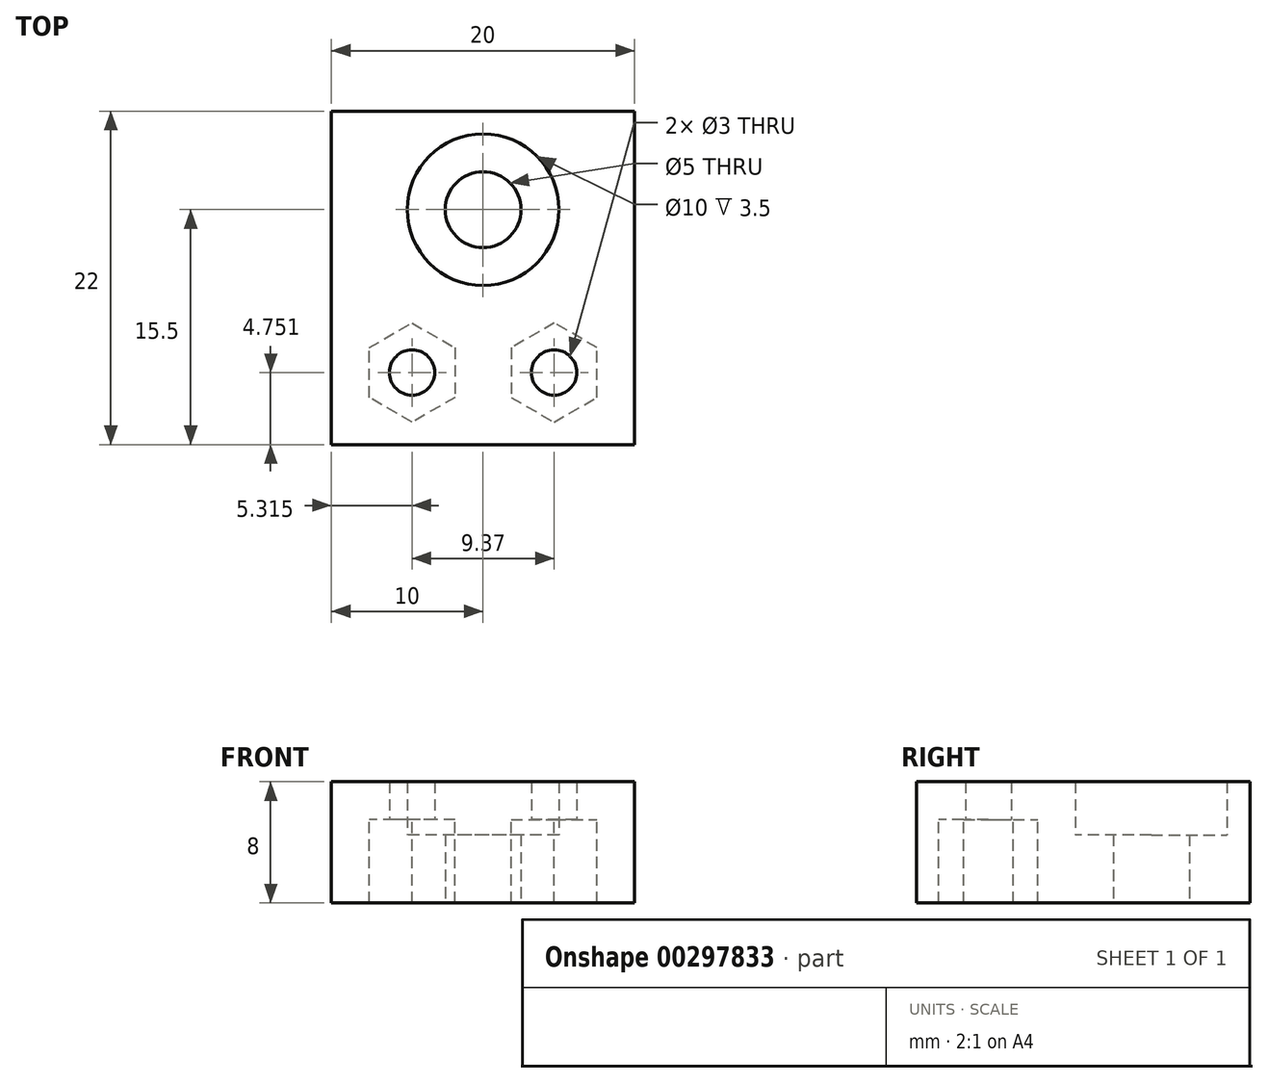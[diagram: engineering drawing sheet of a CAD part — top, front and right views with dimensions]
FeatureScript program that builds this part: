
annotation { "Feature Type Name" : "Feature", "Feature Type Description" : "" }
export const myFeature = defineFeature(function(context is Context, id is Id, definition is map)
    precondition{}
    {
        {
            var Q0;
            Q0=qCreatedBy(makeId("Front.planeOp"),FACE);
            var sketch = newSketch(context, id + "F0", { "sketchPlane" : qUnion([Q0])});
            skLineSegment(sketch, "E0.bottom", {"start": v(10, -4) * mm, "end": v(-10, -4) * mm});
            skLineSegment(sketch, "E0.top", {"start": v(10, 4) * mm, "end": v(-10, 4) * mm});
            skLineSegment(sketch, "E0.left", {"start": v(10, -4) * mm, "end": v(10, 4) * mm});
            skLineSegment(sketch, "E0.right", {"start": v(-10, -4) * mm, "end": v(-10, 4) * mm});
            skPoint(sketch, "E0.middle", {"position": v(0, 0) * mm});
            skLineSegment(sketch, "E1.bottom", {"start": v(-3, -4) * mm, "end": v(3, -4) * mm});
            skLineSegment(sketch, "E1.top", {"start": v(-3, -5.5) * mm, "end": v(3, -5.5) * mm});
            skLineSegment(sketch, "E1.left", {"start": v(-3, -4) * mm, "end": v(-3, -5.5) * mm});
            skLineSegment(sketch, "E1.right", {"start": v(3, -4) * mm, "end": v(3, -5.5) * mm});
            skSolve(sketch);
        }
        {
            var Q0;
            Q0=makeQuery(id+"F0.imprint","IMPRINT",FACE,{"disambiguationData":[TD([[makeQuery(id+"F0.imprint","IMPRINT",EDGE,{"derivedFrom":sQuery(id+"F0.wireOp",EDGE,"E1.bottom")}),-1.0]])]});
            var Q1;
            Q1=makeQuery(id+"F0.imprint","IMPRINT",FACE,{"disambiguationData":[TD([[makeQuery(id+"F0.imprint","IMPRINT",EDGE,{"derivedFrom":sQuery(id+"F0.wireOp",EDGE,"E0.top")}),1.0]])]});
            extrude(context, id + "F1", {"entities" : qUnion([Q0, Q1]), "depth" : 22 * mm});
        }
        {
            var Q0;
            Q0=qCreatedBy(makeId("Top.planeOp"),FACE);
            var sketch = newSketch(context, id + "F2", { "sketchPlane" : qUnion([Q0])});
            skCircle(sketch, "E2", {"center": v(0, -6.5) * mm, "radius": 2.5 * mm});
            skCircle(sketch, "E3", {"center": v(0, -6.5) * mm, "radius": 5 * mm});
            skCircle(sketch, "E4.cCircle", {"center": v(4.68, -17.25) * mm, "radius": 2.83 * mm, "construction": true});
            skLineSegment(sketch, "E4.0", {"start": v(7.52, -15.61) * mm, "end": v(7.52, -18.89) * mm});
            skLineSegment(sketch, "E4.1", {"start": v(7.52, -18.89) * mm, "end": v(4.68, -20.52) * mm});
            skLineSegment(sketch, "E4.2", {"start": v(4.68, -20.52) * mm, "end": v(1.85, -18.89) * mm});
            skLineSegment(sketch, "E4.3", {"start": v(1.85, -18.89) * mm, "end": v(1.85, -15.61) * mm});
            skLineSegment(sketch, "E4.4", {"start": v(1.85, -15.61) * mm, "end": v(4.68, -13.98) * mm});
            skLineSegment(sketch, "E4.5", {"start": v(4.68, -13.98) * mm, "end": v(7.52, -15.61) * mm});
            skPoint(sketch, "E4.0.midPoint", {"position": v(7.52, -17.25) * mm});
            skCircle(sketch, "E5.MirrorC", {"center": v(-4.68, -17.25) * mm, "radius": 2.83 * mm, "construction": true});
            skLineSegment(sketch, "E6.MirrorCS", {"start": v(-1.85, -15.61) * mm, "end": v(-4.69, -13.98) * mm});
            skLineSegment(sketch, "E7.MirrorCS", {"start": v(-4.68, -13.98) * mm, "end": v(-7.52, -15.61) * mm});
            skLineSegment(sketch, "E8.MirrorCS", {"start": v(-7.52, -15.61) * mm, "end": v(-7.52, -18.89) * mm});
            skLineSegment(sketch, "E9.MirrorCS", {"start": v(-7.52, -18.89) * mm, "end": v(-4.68, -20.52) * mm});
            skLineSegment(sketch, "E10.MirrorCS", {"start": v(-4.68, -20.52) * mm, "end": v(-1.85, -18.89) * mm});
            skLineSegment(sketch, "E11.MirrorCS", {"start": v(-1.85, -18.89) * mm, "end": v(-1.85, -15.61) * mm});
            skCircle(sketch, "E12", {"center": v(-4.68, -17.25) * mm, "radius": 1.5 * mm});
            skCircle(sketch, "E13", {"center": v(4.68, -17.25) * mm, "radius": 1.5 * mm});
            skCircle(sketch, "E14", {"center": v(0, -6.5) * mm, "radius": 4 * mm});
            skSolve(sketch);
        }
        {
            var Q0;
            Q0=makeQuery(id+"F2.imprint","IMPRINT",FACE,{"disambiguationData":[TD([[makeQuery(id+"F2.imprint","IMPRINT",EDGE,{"derivedFrom":sQuery(id+"F2.wireOp",EDGE,"E2")}),1.0]])]});
            extrude(context, id + "F3", {"entities" : qUnion([Q0]), "operationType" : NewBodyOperationType.REMOVE, "depth" : 25 * mm, "hasSecondDirection" : true, "secondDirectionOppositeDirection" : true, "secondDirectionDepth" : 25 * mm});
        }
        {
            var Q0;
            Q0=makeQuery(id+"F2.imprint","IMPRINT",FACE,{"disambiguationData":[TD([[makeQuery(id+"F2.imprint","IMPRINT",EDGE,{"derivedFrom":sQuery(id+"F2.wireOp",EDGE,"E3")}),1.0]])]});
            var Q1;
            Q1=makeQuery(id+"F2.imprint","IMPRINT",FACE,{"disambiguationData":[TD([[makeQuery(id+"F2.imprint","IMPRINT",EDGE,{"derivedFrom":sQuery(id+"F2.wireOp",EDGE,"E2")}),-1.0]])]});
            extrude(context, id + "F4", {"entities" : qUnion([Q0, Q1]), "operationType" : NewBodyOperationType.REMOVE, "depth" : 25 * mm, "hasSecondDirection" : true, "secondDirectionOppositeDirection" : false, "secondDirectionDepth" : .5 * mm});
        }
        {
            var Q0;
            Q0=makeQuery(id+"F2.imprint","IMPRINT",FACE,{"disambiguationData":[TD([[makeQuery(id+"F2.imprint","IMPRINT",EDGE,{"derivedFrom":sQuery(id+"F2.wireOp",EDGE,"E12")}),1.0]])]});
            var Q1;
            Q1=makeQuery(id+"F2.imprint","IMPRINT",FACE,{"disambiguationData":[TD([[makeQuery(id+"F2.imprint","IMPRINT",EDGE,{"derivedFrom":sQuery(id+"F2.wireOp",EDGE,"E13")}),1.0]])]});
            extrude(context, id + "F5", {"entities" : qUnion([Q0, Q1]), "operationType" : NewBodyOperationType.REMOVE, "depth" : 25 * mm, "hasSecondDirection" : true, "secondDirectionOppositeDirection" : true, "secondDirectionDepth" : 25 * mm});
        }
        {
            var Q0;
            Q0=makeQuery(id+"F2.imprint","IMPRINT",FACE,{"disambiguationData":[TD([[makeQuery(id+"F2.imprint","IMPRINT",EDGE,{"derivedFrom":sQuery(id+"F2.wireOp",EDGE,"E6.MirrorCS")}),1.0]])]});
            var Q1;
            Q1=makeQuery(id+"F2.imprint","IMPRINT",FACE,{"disambiguationData":[TD([[makeQuery(id+"F2.imprint","IMPRINT",EDGE,{"derivedFrom":sQuery(id+"F2.wireOp",EDGE,"E4.0")}),-1.0]])]});
            extrude(context, id + "F6", {"entities" : qUnion([Q0, Q1]), "operationType" : NewBodyOperationType.REMOVE, "oppositeDirection" : true, "depth" : 25 * mm, "hasSecondDirection" : true, "secondDirectionOppositeDirection" : false, "secondDirectionDepth" : 1.5 * mm});
        }
        {
            var Q0;
            Q0=makeQuery(id+"F2.imprint","IMPRINT",FACE,{"disambiguationData":[TD([[makeQuery(id+"F2.imprint","IMPRINT",EDGE,{"derivedFrom":sQuery(id+"F2.wireOp",EDGE,"E2")}),-1.0]])]});
            extrude(context, id + "F7", {"entities" : qUnion([Q0]), "operationType" : NewBodyOperationType.REMOVE, "oppositeDirection" : true, "depth" : 25 * mm, "hasSecondDirection" : true, "secondDirectionOppositeDirection" : true, "secondDirectionDepth" : 4 * mm});
        }
    });
